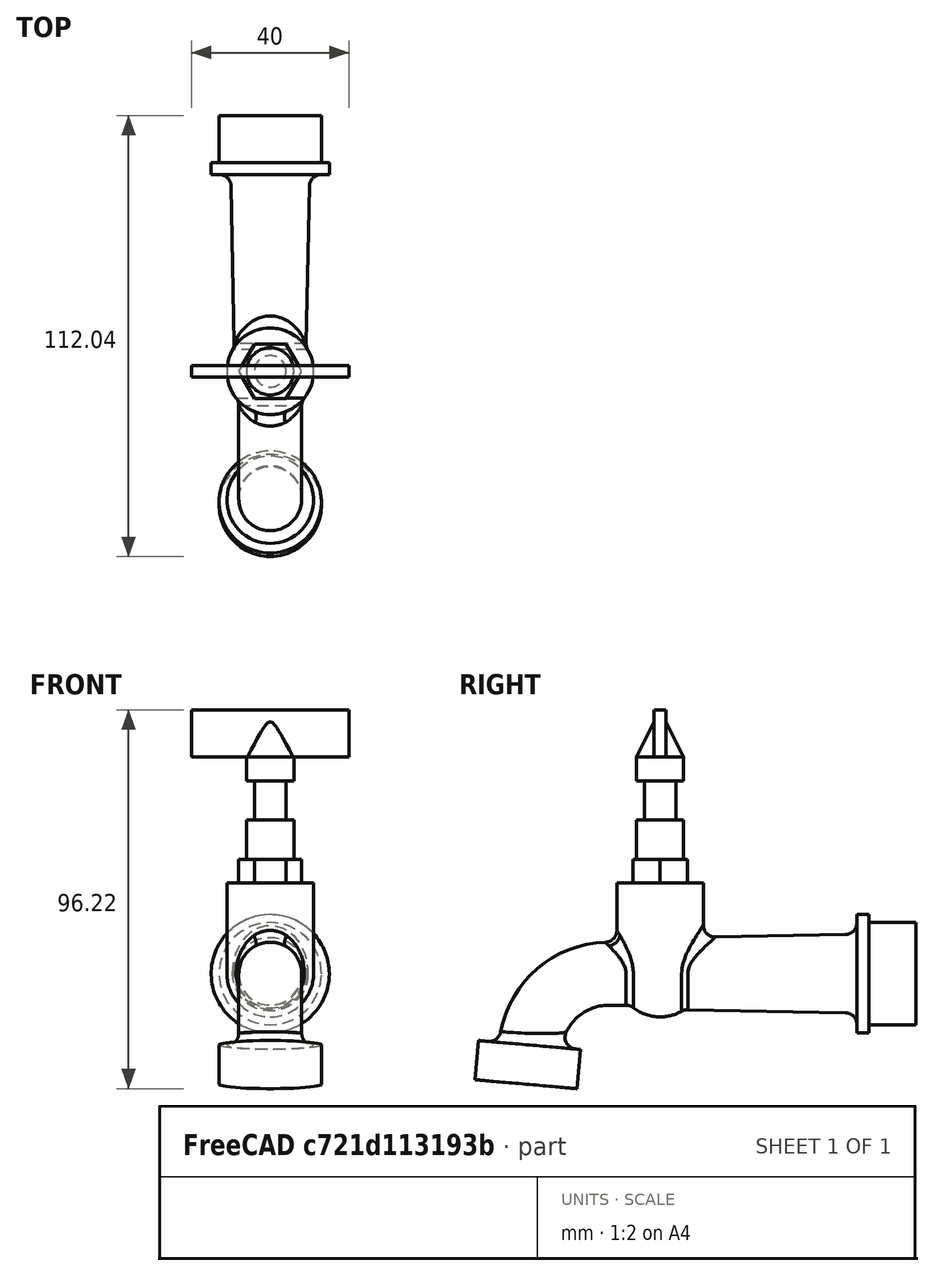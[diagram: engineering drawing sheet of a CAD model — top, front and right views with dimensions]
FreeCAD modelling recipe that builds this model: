
FCSTD DOCUMENT  (FreeCAD 0.18R14555 (Git shallow))
Label: FREECAD #38 - TORNEIRA
License: All rights reserved
LicenseURL: http://en.wikipedia.org/wiki/All_rights_reserved
objects: Part::Cylinder×9, Part::Cone×2, Part::Sphere×1, Part::RegularPolygon×1, Part::Extrusion×1, Part::Box×1, Part::Torus×1, Part::MultiFuse×1, Part::Fillet×1
note: 18 computed .brp shape members not serialized (recipe doc carries the construction recipe); baked Part::Feature solids carry a one-line shape summary decoded from their .brp

FEATURE [Part::Sphere] Sphere
  Angle1 = -90
  Angle2 = 90
  Angle3 = 360
  AttacherType = Attacher::AttachEngine3D
  Radius = 11
FEATURE [Part::Cylinder] Cylinder
  Angle = 360
  AttacherType = Attacher::AttachEngine3D
  Height = 20
  Radius = 11
FEATURE [Part::Cylinder] Cylinder001
  Angle = 360
  AttacherType = Attacher::AttachEngine3D
  Height = 3
  Placement = pos=(0,0,20) rot=(0,0,1;0rad)
  Radius = 11
FEATURE [Part::RegularPolygon] RegularPolygon  label="Regular polygon"
  AttacherType = Attacher::AttachEngine3D
  Circumradius = 8
  Placement = pos=(0,0,23) rot=(0,0,1;0rad)
  Polygon = 6
FEATURE [Part::Extrusion] Extrude
  Base = -> RegularPolygon
  Dir = (0,0,1)
  DirMode = 2
  FaceMakerClass = Part::FaceMakerBullseye
  LengthFwd = 6
  LengthRev = 0
  Solid = true
  Symmetric = false
FEATURE [Part::Cylinder] Cylinder002
  Angle = 360
  AttacherType = Attacher::AttachEngine3D
  Height = 10
  Placement = pos=(0,0,29) rot=(0,0,1;0rad)
  Radius = 6
FEATURE [Part::Cylinder] Cylinder003
  Angle = 360
  AttacherType = Attacher::AttachEngine3D
  Height = 10
  Placement = pos=(0,0,39) rot=(0,0,1;0rad)
  Radius = 4
FEATURE [Part::Cylinder] Cylinder004
  Angle = 360
  AttacherType = Attacher::AttachEngine3D
  Height = 6
  Placement = pos=(0,0,49) rot=(0,0,1;0rad)
  Radius = 6
FEATURE [Part::Cone] Cone
  Angle = 360
  AttacherType = Attacher::AttachEngine3D
  Height = 10
  Placement = pos=(0,0,55) rot=(0,0,1;0rad)
  Radius1 = 6
  Radius2 = 1
FEATURE [Part::Box] Box  label="Cube"
  AttacherType = Attacher::AttachEngine3D
  Height = 12
  Length = 40
  Placement = pos=(-20,-1.5,55) rot=(0,0,1;0rad)
  Width = 3
FEATURE [Part::Cone] Cone001
  Angle = 360
  AttacherType = Attacher::AttachEngine3D
  Height = 50
  Placement = pos=(0,0,0) rot=(-1,0,0;1.5708rad)
  Radius1 = 9
  Radius2 = 10
FEATURE [Part::Cylinder] Cylinder005
  Angle = 360
  AttacherType = Attacher::AttachEngine3D
  Height = 3
  Placement = pos=(0,50,-1.1e-14) rot=(-1,0,0;1.5708rad)
  Radius = 15
FEATURE [Part::Cylinder] Cylinder006
  Angle = 360
  AttacherType = Attacher::AttachEngine3D
  Height = 12
  Placement = pos=(0,53,-1.2e-14) rot=(-1,0,0;1.5708rad)
  Radius = 13
FEATURE [Part::Cylinder] Cylinder007
  Angle = 360
  AttacherType = Attacher::AttachEngine3D
  Height = 10
  Placement = pos=(0,-3,-1e-15) rot=(1,0,0;1.5708rad)
  Radius = 8
FEATURE [Part::Torus] Torus
  Angle1 = -180
  Angle2 = 180
  Angle3 = 85
  AttacherType = Attacher::AttachEngine3D
  Placement = pos=(-3e-15,-13,-20) rot=(0.707107,0,0.707107;3.14159rad)
  Radius1 = 20
  Radius2 = 8
FEATURE [Part::Cylinder] Cylinder008
  Angle = 360
  AttacherType = Attacher::AttachEngine3D
  Height = 10
  Placement = pos=(0,-34.091,-28.0834) rot=(-1,0,0;0.087266rad)
  Radius = 13
FEATURE [Part::MultiFuse] Fusion
  Shapes = -> [Cylinder008,Torus,Cylinder007,Cylinder006,Cylinder005,Cone001,Box,Cone,Cylinder004,Cylinder003,Cylinder002,Extrude,Cylinder001,Cylinder,Sphere]
FEATURE [Part::Fillet] Fillet
  Base = -> Fusion
  Edges = 6 edges r=3: [Edge4,Edge9,Edge10,Edge12,Edge18,Edge21]
